SOLIDWORKS PART (.sldprt)
format: sldprt  version: not decoded by parser v0  size: 303,104 bytes
history: native  units: mm
features: sketch x8, cut_revolve x3, cut_extrude x3, pattern_linear x2, material x1, revolve x1, plane x1, extrude x1, fillet x1 (+12 scaffold rows collapsed)
feature tree (33):
  scaffold x12  (default folders/planes/origin — collapsed)
  material  "Material <not specified>"
  sketch  "Sketch1"  dims[Thread Dia=2.8448mm Screw Length=228.6mm Length=6.35mm Head Height=2.1082mm D1=4.2418mm]
  revolve  "Revolve1"  Angle=360deg
  plane  "Plane1"
  sketch  "Sketch2"  dims[c1.Thread Pitch=0.635mm c1.D2=~0.079375mm c1.D3=~0.15875mm c1.D4=0.635mm c1.D1=~12.704307mm c2.D1=60.0deg c2.Thread Length=298.45mm c2.Min Thread Length=190.5mm c2.D5=~294.890463mm c2.D6=~292.121934mm c3.D5=90.0deg c4.D5=190.5mm c4.D6=90.0deg c4.Thread Length=298.45mm c5.D5=~4.763642deg c5.Min Thread Length=50.8mm]
  cut_revolve  "Cut-Revolve1"  Angle=360deg
  sketch  "Sketch3"  dims[c1.D1=~17.969819mm c2.D1=20.0deg c2.D2=2.8448mm]
  cut_revolve  "Cut-Revolve2"  Angle=360deg
  pattern_linear  "LPattern1"  Count1=7 Count2=1 Spacing1=0.635mm Spacing2=50mm
  pattern_linear  "LPattern2"  Count1=2 Count2=1 Spacing1=0.635mm Spacing2=50mm
  sketch  "Sketch4"  dims[Head Dia=6.477mm]
  extrude  "Extrude1"  [1 undecoded]
  sketch  "Sketch9"  dims[c1.D2=~0.770447mm c1.D4=0.127mm c1.D1=~9.560296mm c2.D1=82.0deg c2.D2=0.508mm c2.D3=0.508mm]
  cut_revolve  "Cut-Revolve3"  Angle=360deg
  fillet  "Fillet1"  Radius=0.0508mm
  sketch  "Sketch6"  dims[Hex=1.5875mm]
  cut_extrude  "Cut-Extrude1"  Depth=1.0541mm
  sketch  "Sketch7"
  cut_extrude  "Cut-Extrude4"  Depth=1.0541mm
  sketch  "Sketch8"
  cut_extrude  "Cut-Extrude5"  Depth=0.351367mm
decode coverage: 16 of 19 modeling features carry decoded parameters
note: ~ marks probable driven/reference dimensions
note: 1 parameter value undecoded
note: suppression state not decoded; provenance and decode notes live in map.json
